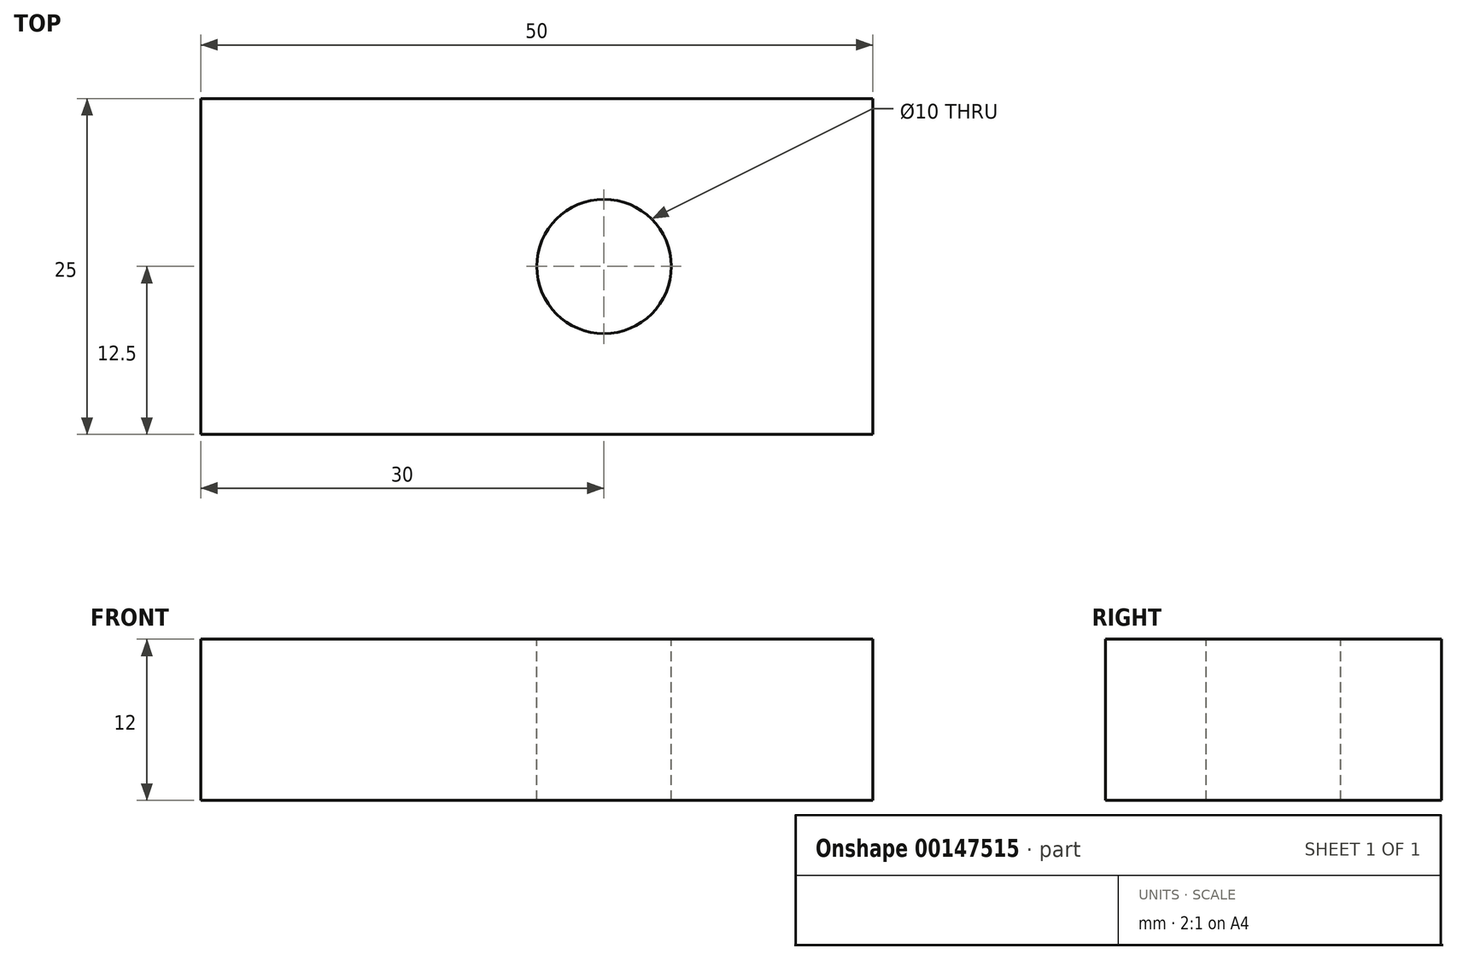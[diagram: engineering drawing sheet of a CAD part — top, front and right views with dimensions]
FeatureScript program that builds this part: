
annotation { "Feature Type Name" : "Feature", "Feature Type Description" : "" }
export const myFeature = defineFeature(function(context is Context, id is Id, definition is map)
    precondition{}
    {
        {
            var Q0;
            Q0=qCreatedBy(makeId("Front.planeOp"),FACE);
            var sketch = newSketch(context, id + "F0", { "sketchPlane" : qUnion([Q0])});
            skLineSegment(sketch, "E0.bottom", {"start": v(0, 0) * mm, "end": v(50, 0) * mm});
            skLineSegment(sketch, "E0.top", {"start": v(0, 12) * mm, "end": v(50, 12) * mm});
            skLineSegment(sketch, "E0.left", {"start": v(0, 0) * mm, "end": v(0, 12) * mm});
            skLineSegment(sketch, "E0.right", {"start": v(50, 0) * mm, "end": v(50, 12) * mm});
            skSolve(sketch);
        }
        {
            var Q0;
            Q0 = qSketchRegion(id + "F0", true);
            extrude(context, id + "F1", {"entities" : qUnion([Q0]), "endBound" : BoundingType.SYMMETRIC, "depth" : 25 * mm});
        }
        {
            var Q0;
            Q0=makeQuery(id+"F1.opExtrude","SWEPT_FACE",FACE,{"disambiguationData":[OSD([sQuery(id+"F0.wireOp",EDGE,"E0.top")])]});
            var sketch = newSketch(context, id + "F2", { "sketchPlane" : qUnion([Q0])});
            skCircle(sketch, "E1", {"center": v(30, 0) * mm, "radius": 5 * mm});
            skSolve(sketch);
        }
        {
            var Q0;
            Q0=makeQuery(id+"F2.imprint","IMPRINT",FACE,{"disambiguationData":[TD([[makeQuery(id+"F2.imprint","IMPRINT",EDGE,{"derivedFrom":sQuery(id+"F2.wireOp",EDGE,"E1")}),1.0]])]});
            var Q1;
            Q1=sQuery(id+"F2.wireOp",EDGE,"E1");
            extrude(context, id + "F3", {"entities" : qUnion([Q0]), "operationType" : NewBodyOperationType.REMOVE, "surfaceEntities" : qUnion([Q1]), "oppositeDirection" : true, "depth" : 25 * mm});
        }
    });
